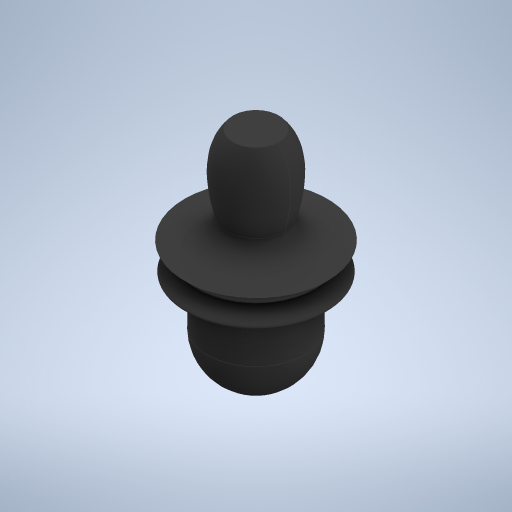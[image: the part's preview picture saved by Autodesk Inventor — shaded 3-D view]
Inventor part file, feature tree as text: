
AUTODESK INVENTOR PART (.ipt)
format: ipt  version: 2023 (Build 270158000, 158)  size: 445,952 bytes
history: native  units: in
note: dims shown in document units (in); Inventor stores cm internally (conversion verified against a paired STEP export)
features: revolve x2, sketch x2
ambient origin geometry x8: Origin, YZ Plane, XZ Plane, XY Plane, X Axis, Y Axis, Z Axis, Center Point
bodies: Solid1 (feature_tree)
feature tree (4):
  revolve  "Revolution1"  [1 undecoded]
  revolve  "Revolution2"  [1 undecoded]
  sketch  "Sketch1"  dims[d0=0.6693in d1=0.5906in]
  sketch  "Sketch2"  dims[d3=0.4455in d5=2.3574in d6=0.1271in d7=0.315in d8=1.0236in d9=0.1672in d10=0.1497in d13=0.3725in d14=0.3993in d15=90.0deg d16=90.0deg]
note: 2 required parameter values undecoded (feature->parameter linkage not recoverable at this tier; creation-order binding heuristic only, values carry confidence <= 0.55)
